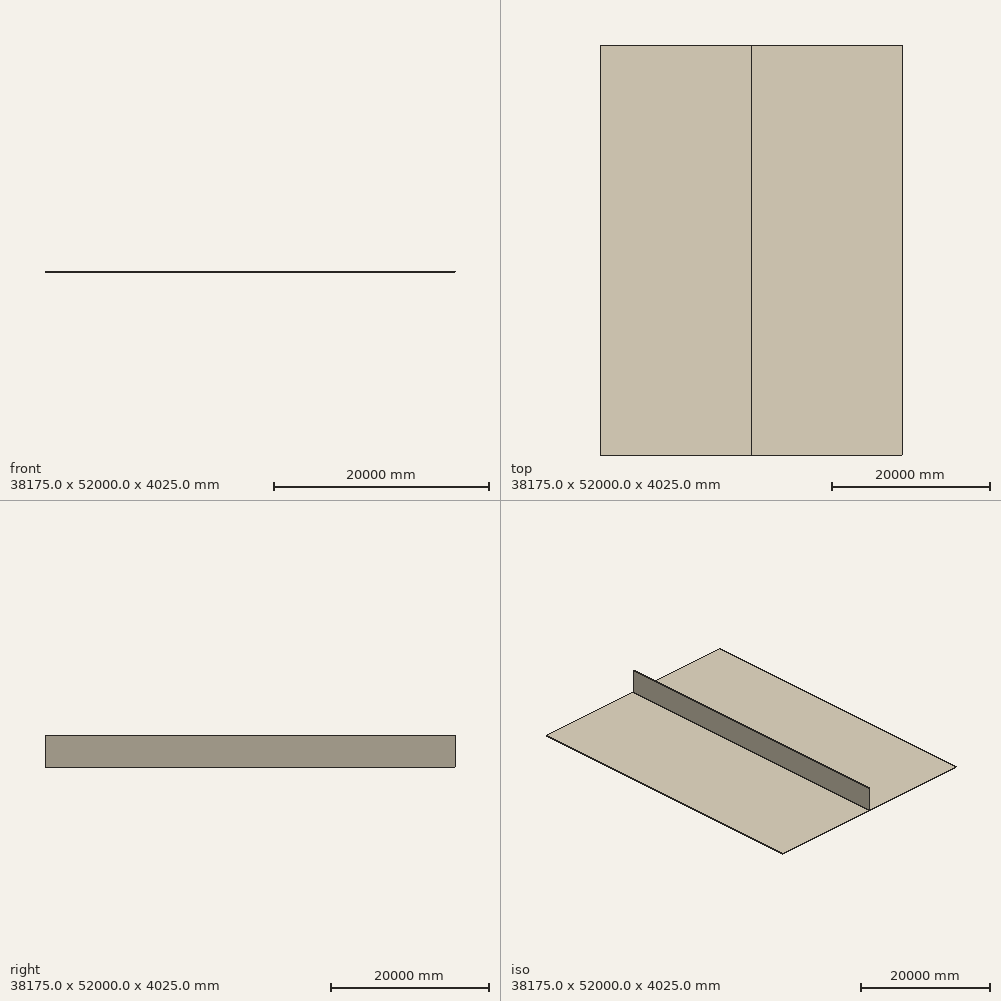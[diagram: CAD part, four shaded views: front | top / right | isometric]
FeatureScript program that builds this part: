
annotation { "Feature Type Name" : "Feature", "Feature Type Description" : "" }
export const myFeature = defineFeature(function(context is Context, id is Id, definition is map)
    precondition{}
    {
        {
            var Q0;
            Q0=qCreatedBy(makeId("Top.planeOp"),FACE);
            var sketch = newSketch(context, id + "F0", { "sketchPlane" : qUnion([Q0])});
            skLineSegment(sketch, "E0.bottom", {"start": v(19087.5, 26000) * mm, "end": v(-19087.5, 26000) * mm});
            skLineSegment(sketch, "E0.top", {"start": v(19087.5, -26000) * mm, "end": v(-19087.5, -26000) * mm});
            skLineSegment(sketch, "E0.left", {"start": v(19087.5, 26000) * mm, "end": v(19087.5, -26000) * mm});
            skLineSegment(sketch, "E0.right", {"start": v(-19087.5, 26000) * mm, "end": v(-19087.5, -26000) * mm});
            skPoint(sketch, "E0.middle", {"position": v(0, 0) * mm});
            skSolve(sketch);
        }
        {
            var Q0;
            Q0 = qSketchRegion(id + "F0", true);
            extrude(context, id + "F1", {"entities" : qUnion([Q0]), "oppositeDirection" : true, "depth" : 25 * mm, "offsetDistance" : 25 * mm});
        }
        {
            var Q0;
            Q0=qCreatedBy(makeId("Top.planeOp"),FACE);
            var sketch = newSketch(context, id + "F2", { "sketchPlane" : qUnion([Q0])});
            skLineSegment(sketch, "E1.bottom", {"start": v(25, 26000) * mm, "end": v(-25, 26000) * mm});
            skLineSegment(sketch, "E1.top", {"start": v(25, -26000) * mm, "end": v(-25, -26000) * mm});
            skLineSegment(sketch, "E1.left", {"start": v(25, 26000) * mm, "end": v(25, -26000) * mm});
            skLineSegment(sketch, "E1.right", {"start": v(-25, 26000) * mm, "end": v(-25, -26000) * mm});
            skPoint(sketch, "E1.middle", {"position": v(0, 0) * mm});
            skSolve(sketch);
        }
        {
            var Q0;
            Q0 = qSketchRegion(id + "F2", true);
            extrude(context, id + "F3", {"entities" : qUnion([Q0]), "operationType" : NewBodyOperationType.ADD, "depth" : 4000 * mm, "offsetDistance" : 25 * mm});
        }
    });
